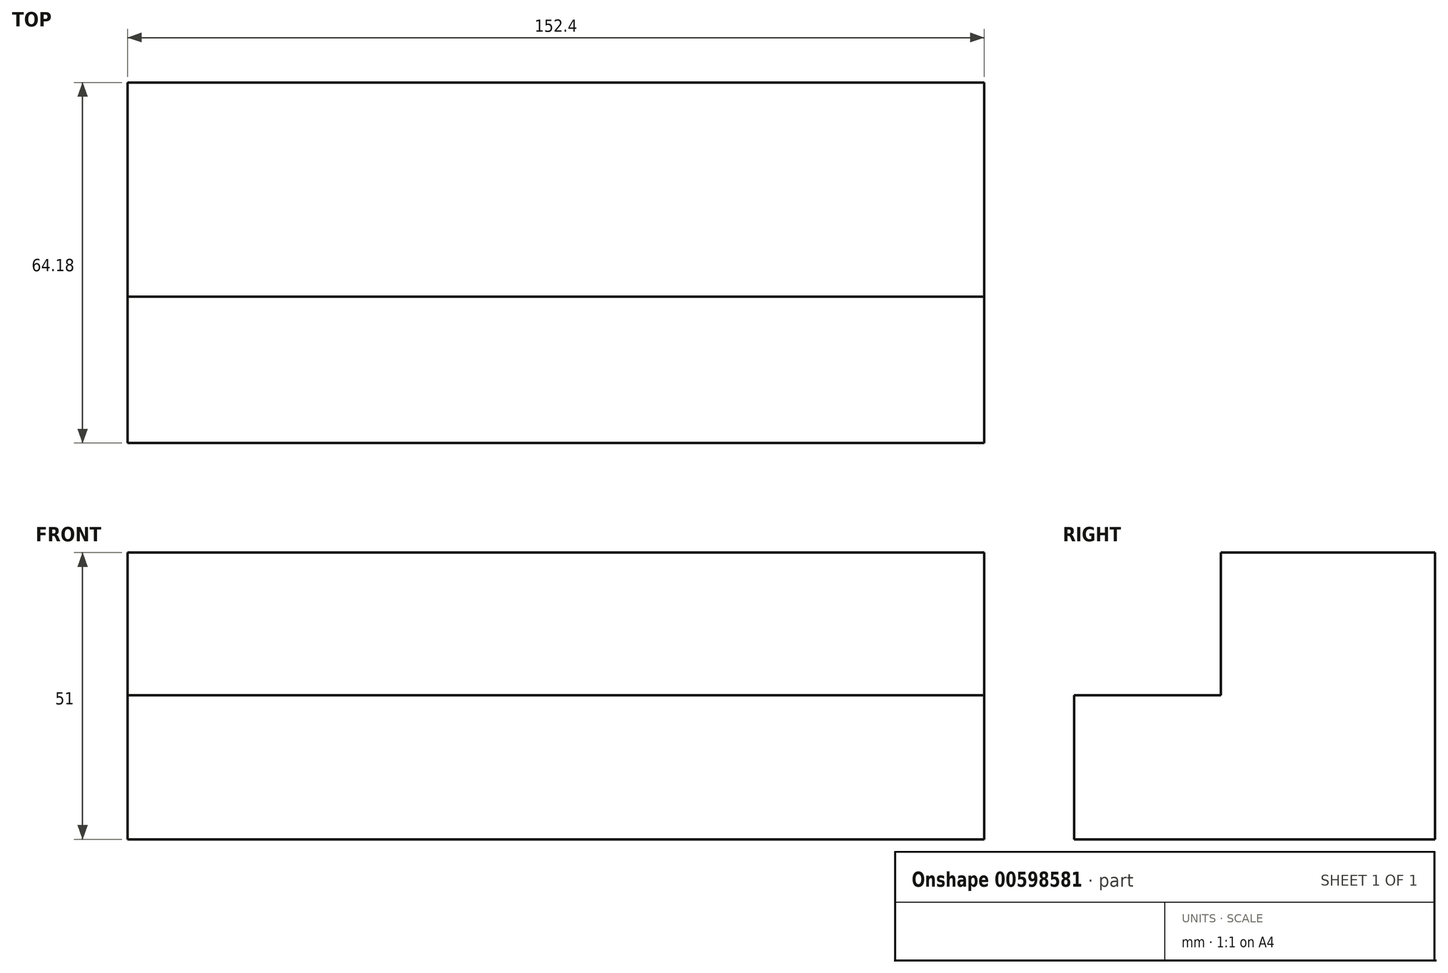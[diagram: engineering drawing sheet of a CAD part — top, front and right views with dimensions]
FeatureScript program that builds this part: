
annotation { "Feature Type Name" : "Feature", "Feature Type Description" : "" }
export const myFeature = defineFeature(function(context is Context, id is Id, definition is map)
    precondition{}
    {
        {
            var Q0;
            Q0=qCreatedBy(makeId("Right.planeOp"),FACE);
            var sketch = newSketch(context, id + "F0", { "sketchPlane" : qUnion([Q0])});
            skLineSegment(sketch, "E0", {"start": v(0, 0) * mm, "end": v(-38.25, 0) * mm});
            skLineSegment(sketch, "E1", {"start": v(-38.25, 0) * mm, "end": v(-38.25, 25.6) * mm});
            skLineSegment(sketch, "E2", {"start": v(-38.25, 25.6) * mm, "end": v(-12.17, 25.6) * mm});
            skLineSegment(sketch, "E3", {"start": v(-12.17, 25.6) * mm, "end": v(-12.17, 51) * mm});
            skLineSegment(sketch, "E4", {"start": v(-12.17, 51) * mm, "end": v(25.93, 51) * mm});
            skLineSegment(sketch, "E5", {"start": v(25.93, 51) * mm, "end": v(25.93, 0) * mm});
            skLineSegment(sketch, "E6", {"start": v(25.93, 0) * mm, "end": v(0, 0) * mm});
            skSolve(sketch);
        }
        {
            var Q0;
            Q0=makeQuery(id+"F0.imprint","IMPRINT",FACE,{"disambiguationData":[TD([[makeQuery(id+"F0.imprint","IMPRINT",EDGE,{"derivedFrom":sQuery(id+"F0.wireOp",EDGE,"E0")}),-1.0]])]});
            extrude(context, id + "F1", {"entities" : qUnion([Q0]), "depth" : 76.2 * mm, "offsetDistance" : 25.4 * mm});
        }
        {
            var Q0;
            Q0=makeQuery(id+"F1.opExtrude","CAP_FACE",FACE,{"disambiguationData":[OSD([sQuery(id+"F0.wireOp",EDGE,"E0"),sQuery(id+"F0.wireOp",EDGE,"E1"),sQuery(id+"F0.wireOp",EDGE,"E2"),sQuery(id+"F0.wireOp",EDGE,"E3"),sQuery(id+"F0.wireOp",EDGE,"E4"),sQuery(id+"F0.wireOp",EDGE,"E5"),sQuery(id+"F0.wireOp",EDGE,"E6")])],"isStart":true});
            extrude(context, id + "F2", {"entities" : qUnion([Q0]), "operationType" : NewBodyOperationType.ADD, "depth" : 76.2 * mm, "offsetDistance" : 25.4 * mm});
        }
    });
